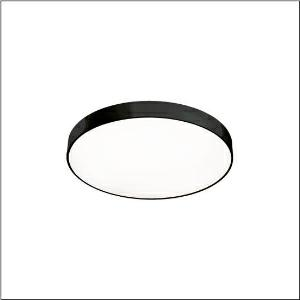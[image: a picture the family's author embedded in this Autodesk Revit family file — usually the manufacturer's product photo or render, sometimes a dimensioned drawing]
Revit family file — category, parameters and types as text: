
# Revit family: round_21_m_51mr36gm8321b
name_source: partatom
category: Lighting Fixtures
units: mm (PartAtom-declared; Revit-internal decimal feet)

## family parameters
Cut with Voids When Loaded = No
Host = Face
Light Source = No
Part Type = Normal
Room Calculation Point = No
Round Connector Dimension = Use Diameter
Shared = No

## types (1)
- --- (1 x LED, 7820 lm, 60.8 W, 3000K)
    Apparent Load = 61 VA
    CIE Flux Codes = 49 80 96 85 100
    Color Rendering = 80
    Color Temperature = 3000K
    Default Elevation = 1800 mm
    Description = Round 21 M, wall and ceiling luminaire, primary optical cover: cover, of PMMA, opal, light emission: direct/indirect distribution, primary light characteristic: symmetric, installation type: suspended mounting, surface-mounted, LED, rated luminous flux: 7.820lm, luminous efficacy: 129lm/W, light colour: 830, colour temperature: 3000K, with terminal, 3-pole, mains connection: 230V, AC, 50/60Hz, rated input power: 61W, housing, of aluminium, coated, black, diameter: 600mm, height: 62mm, protection rating (complete): IP40, insulation class (complete): insulation class I (protective earthing), certification: CE, impact resistance: IK04, permissible operating ambient temperature: -10..+35°C, packaging unit: 1 piece
    Height = 87 mm
    Lamp = 1 x LED
    Lamp Light Flux = 7820 lm
    Lamp Power = 60.8 W
    Lamp count = 1
    Length = 600 mm
    Luminous efficacy = 129 lm/W
    Manufacturer = Siteco
    ModVariant = No
    Model = 51MR36GM8321B
    Mounting Place = Ceiling
    Mounting Type = Surface mounted
    Number of Poles = 1
    OnlyDefault = Yes
    Power Factor = 1
    Product Name = Round 21 M
    Product group = wall and ceiling luminaire
    ProductGroupID = 301
    Protection Class = Protection class I
    Protection Degree = IP 40
    RLX_Detail_Level = 1
    RLX_Emergency_Light_Flux = 0 lm
    RLX_Emergency_Type = 0
    RLX_Emergency_Type_DB = No
    RlxData = <blob elided: 20773 chars, md5=a9310154>
    Socket = socket
    Standby Power = 0 W
    System Light Flux = 7820 lm
    System Power = 61 W
    Type Comments = factory setting: luminous flux: 100 % | (ON | ON | ON | ON) | 700 mA
    Type Image = l_1258332.jpg
    URL = http://relux.com
    VarID = @adj_013177
    Voltage = 0 V
    Weight = 0.00 kg
    Width = 0 mm  [stored 0 ft]

note: [stored X ft] marks values corroborated as IEEE doubles in the binary element streams (Revit-internal decimal feet)

## geometry (parser evidence)
native form markers: Blend x4, Sweep x13
no freeform markers — native parametric forms only
